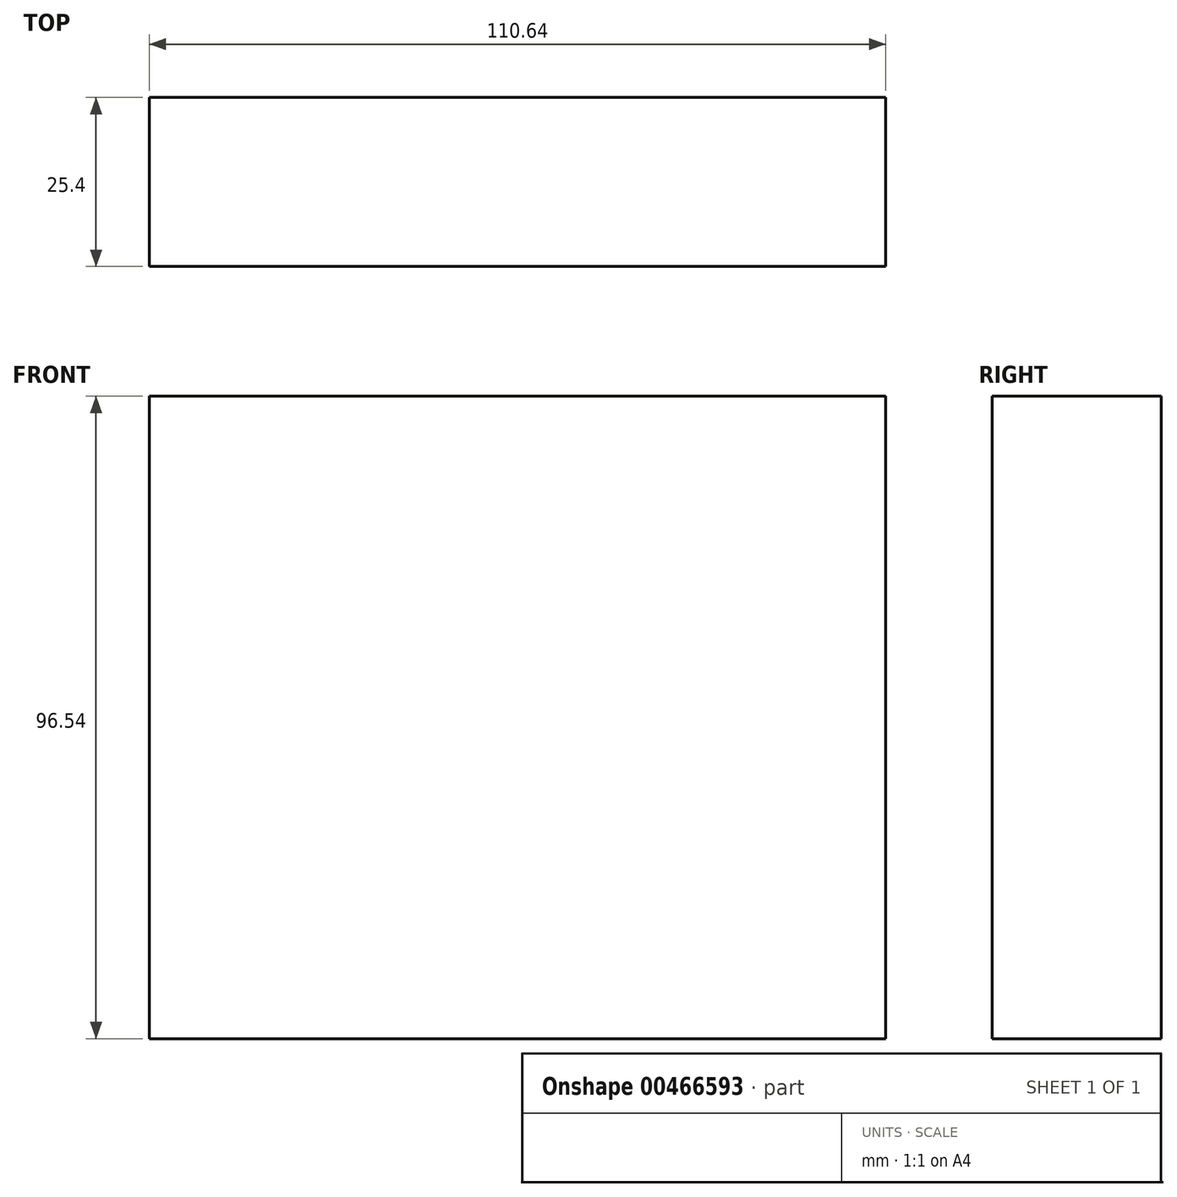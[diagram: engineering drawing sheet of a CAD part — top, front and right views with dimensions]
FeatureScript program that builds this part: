
annotation { "Feature Type Name" : "Feature", "Feature Type Description" : "" }
export const myFeature = defineFeature(function(context is Context, id is Id, definition is map)
    precondition{}
    {
        {
            var Q0;
            Q0=qCreatedBy(makeId("Front.planeOp"),FACE);
            var sketch = newSketch(context, id + "F0", { "sketchPlane" : qUnion([Q0])});
            skLineSegment(sketch, "E0.bottom", {"start": v(55.32, 48.27) * mm, "end": v(-55.32, 48.27) * mm});
            skLineSegment(sketch, "E0.top", {"start": v(55.32, -48.27) * mm, "end": v(-55.32, -48.27) * mm});
            skLineSegment(sketch, "E0.left", {"start": v(55.32, 48.27) * mm, "end": v(55.32, -48.27) * mm});
            skLineSegment(sketch, "E0.right", {"start": v(-55.32, 48.27) * mm, "end": v(-55.32, -48.27) * mm});
            skPoint(sketch, "E0.middle", {"position": v(0, 0) * mm});
            skSolve(sketch);
        }
        {
            var Q0;
            Q0 = qSketchRegion(id + "F0", true);
            extrude(context, id + "F1", {"entities" : qUnion([Q0]), "depth" : 25.4 * mm});
        }
    });
